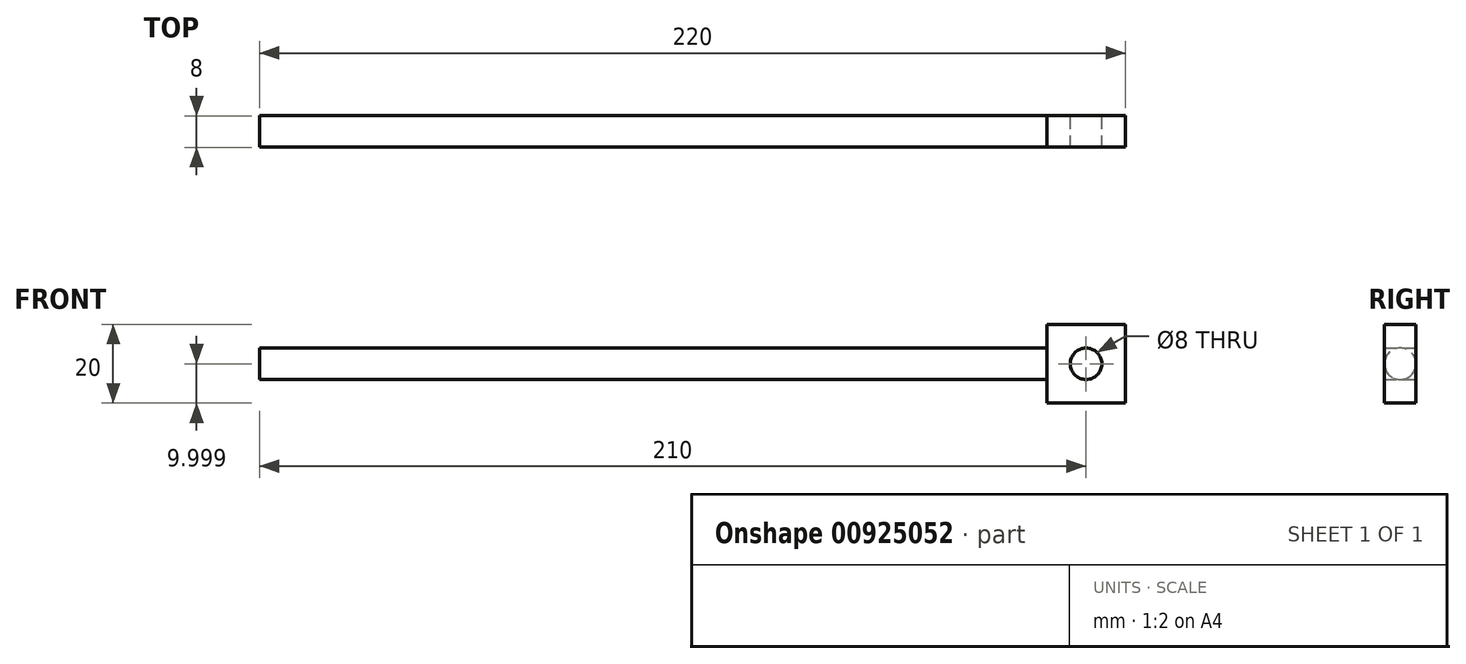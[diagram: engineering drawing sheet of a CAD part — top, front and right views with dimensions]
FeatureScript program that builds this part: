
annotation { "Feature Type Name" : "Feature", "Feature Type Description" : "" }
export const myFeature = defineFeature(function(context is Context, id is Id, definition is map)
    precondition{}
    {
        {
            var Q0;
            Q0=qCreatedBy(makeId("Right.planeOp"),FACE);
            var sketch = newSketch(context, id + "F0", { "sketchPlane" : qUnion([Q0])});
            skCircle(sketch, "E0", {"center": v(-41.78, 63.17) * mm, "radius": 4 * mm});
            skSolve(sketch);
        }
        {
            var Q0;
            Q0=makeQuery(id+"F0.imprint","IMPRINT",FACE,{"disambiguationData":[TD([[makeQuery(id+"F0.imprint","IMPRINT",EDGE,{"derivedFrom":sQuery(id+"F0.wireOp",EDGE,"E0")}),1.0]])]});
            extrude(context, id + "F1", {"entities" : qUnion([Q0]), "depth" : 200 * mm, "offsetDistance" : 25 * mm});
        }
        {
            var Q0;
            Q0=makeQuery(id+"F1.opExtrude","CAP_FACE",FACE,{"disambiguationData":[OSD([sQuery(id+"F0.wireOp",EDGE,"E0")])],"isStart":false});
            var sketch = newSketch(context, id + "F2", { "sketchPlane" : qUnion([Q0])});
            skLineSegment(sketch, "E1.bottom", {"start": v(-45.78, 73.17) * mm, "end": v(-37.78, 73.17) * mm});
            skLineSegment(sketch, "E1.top", {"start": v(-45.78, 53.17) * mm, "end": v(-37.78, 53.17) * mm});
            skLineSegment(sketch, "E1.left", {"start": v(-37.78, 73.17) * mm, "end": v(-37.78, 53.17) * mm});
            skLineSegment(sketch, "E1.right", {"start": v(-45.78, 73.17) * mm, "end": v(-45.78, 53.17) * mm});
            skSolve(sketch);
        }
        {
            var Q0;
            {var subQ0=sQuery(id+"F2.wireOp",EDGE,"E1.bottom");Q0=makeQuery(id+"F2.imprint","IMPRINT",FACE,{"disambiguationData":[TD([[makeQuery(id+"F2.imprint","IMPRINT",EDGE,{"derivedFrom":subQ0}),-1.0]])]});}
            var Q1;
            {var subQ0=makeQuery(id+"F1.opExtrude","CAP_EDGE",EDGE,{"disambiguationData":[OSD([sQuery(id+"F0.wireOp",EDGE,"E0")])],"isStart":false});var subQ1=makeQuery(id+"F2.imprint","INTERSECT",VERTEX,{"derivedFrom":[subQ0,sQuery(id+"F2.wireOp",EDGE,"E1.left")]});Q1=makeQuery(id+"F2.imprint","IMPRINT",FACE,{"disambiguationData":[TD([[makeQuery(id+"F2.imprint","IMPRINT",EDGE,{"disambiguationData":[TD([[subQ1,-1.0]])],"derivedFrom":subQ0}),1.0]])]});}
            var Q2;
            {var subQ0=sQuery(id+"F2.wireOp",EDGE,"E1.top");Q2=makeQuery(id+"F2.imprint","IMPRINT",FACE,{"disambiguationData":[TD([[makeQuery(id+"F2.imprint","IMPRINT",EDGE,{"derivedFrom":subQ0}),1.0]])]});}
            extrude(context, id + "F3", {"entities" : qUnion([Q0, Q1, Q2]), "operationType" : NewBodyOperationType.ADD, "depth" : 20 * mm, "offsetDistance" : 25 * mm});
        }
        {
            var Q0;
            Q0=makeQuery(id+"F3.opExtrude","SWEPT_FACE",FACE,{"disambiguationData":[OSD([sQuery(id+"F2.wireOp",EDGE,"E1.left")])]});
            var sketch = newSketch(context, id + "F4", { "sketchPlane" : qUnion([Q0])});
            skCircle(sketch, "E2", {"center": v(-210, 63.17) * mm, "radius": 4 * mm});
            skSolve(sketch);
        }
        {
            var Q0;
            Q0=makeQuery(id+"F4.imprint","IMPRINT",FACE,{"disambiguationData":[TD([[makeQuery(id+"F4.imprint","IMPRINT",EDGE,{"derivedFrom":sQuery(id+"F4.wireOp",EDGE,"E2")}),1.0]])]});
            extrude(context, id + "F5", {"entities" : qUnion([Q0]), "operationType" : NewBodyOperationType.REMOVE, "oppositeDirection" : true, "depth" : 25 * mm, "offsetDistance" : 25 * mm});
        }
    });
